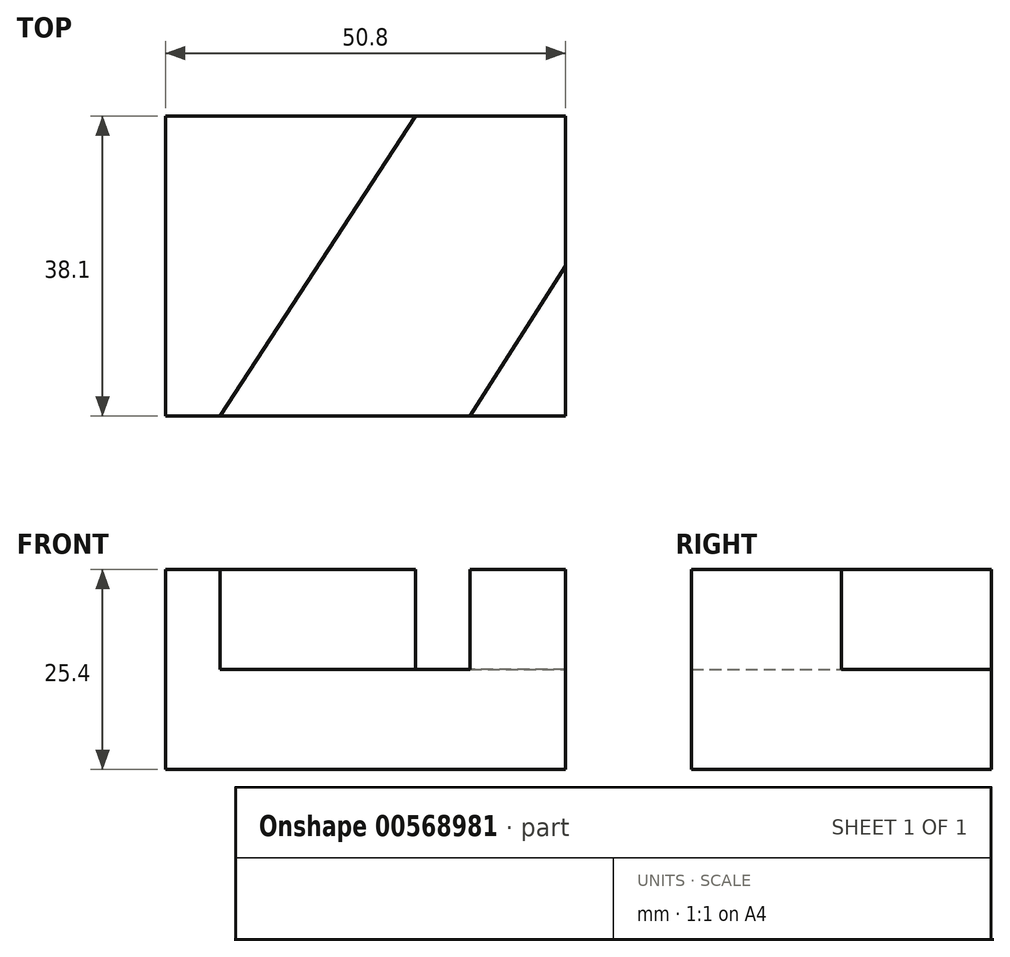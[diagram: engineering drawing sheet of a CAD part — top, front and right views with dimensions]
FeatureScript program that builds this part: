
annotation { "Feature Type Name" : "Feature", "Feature Type Description" : "" }
export const myFeature = defineFeature(function(context is Context, id is Id, definition is map)
    precondition{}
    {
        {
            var Q0;
            Q0=qCreatedBy(makeId("Top.planeOp"),FACE);
            var sketch = newSketch(context, id + "F0", { "sketchPlane" : qUnion([Q0])});
            skLineSegment(sketch, "E0.bottom", {"start": v(-24.31, 27.23) * mm, "end": v(26.49, 27.23) * mm});
            skLineSegment(sketch, "E0.top", {"start": v(-24.31, -10.87) * mm, "end": v(26.49, -10.87) * mm});
            skLineSegment(sketch, "E0.left", {"start": v(-24.31, 27.23) * mm, "end": v(-24.31, -10.87) * mm});
            skLineSegment(sketch, "E0.right", {"start": v(26.49, 27.23) * mm, "end": v(26.49, -10.87) * mm});
            skSolve(sketch);
        }
        {
            var Q0;
            Q0 = qSketchRegion(id + "F0", true);
            extrude(context, id + "F1", {"entities" : qUnion([Q0]), "depth" : 25.4 * mm, "offsetDistance" : 25.4 * mm});
        }
        {
            var Q0;
            Q0=makeQuery(id+"F1.opExtrude","CAP_FACE",FACE,{"disambiguationData":[OSD([sQuery(id+"F0.wireOp",EDGE,"E0.bottom"),sQuery(id+"F0.wireOp",EDGE,"E0.top"),sQuery(id+"F0.wireOp",EDGE,"E0.left"),sQuery(id+"F0.wireOp",EDGE,"E0.right")])],"isStart":false});
            var sketch = newSketch(context, id + "F2", { "sketchPlane" : qUnion([Q0])});
            skLineSegment(sketch, "E1", {"start": v(-17.37, -10.87) * mm, "end": v(7.44, 27.23) * mm});
            skLineSegment(sketch, "E2", {"start": v(7.44, 27.23) * mm, "end": v(26.49, 27.23) * mm});
            skLineSegment(sketch, "E3", {"start": v(26.49, 27.23) * mm, "end": v(26.49, 8.18) * mm});
            skLineSegment(sketch, "E4", {"start": v(26.49, 8.18) * mm, "end": v(14.38, -10.87) * mm});
            skLineSegment(sketch, "E5", {"start": v(14.38, -10.87) * mm, "end": v(-17.37, -10.87) * mm});
            skSolve(sketch);
        }
        {
            var Q0;
            Q0=makeQuery(id+"F2.imprint","IMPRINT",FACE,{"disambiguationData":[TD([[makeQuery(id+"F2.imprint","IMPRINT",EDGE,{"derivedFrom":sQuery(id+"F2.wireOp",EDGE,"E1")}),-1.0]])]});
            var sketch = newSketch(context, id + "F3", { "sketchPlane" : qUnion([Q0])});
            skSolve(sketch);
        }
        {
            var Q0;
            Q0 = qSketchRegion(id + "F3", true);
            var Q1;
            Q1=makeQuery(id+"F2.imprint","IMPRINT",FACE,{"disambiguationData":[TD([[makeQuery(id+"F2.imprint","IMPRINT",EDGE,{"derivedFrom":sQuery(id+"F2.wireOp",EDGE,"E1")}),-1.0]])]});
            extrude(context, id + "F4", {"entities" : qUnion([Q0, Q1]), "operationType" : NewBodyOperationType.REMOVE, "oppositeDirection" : true, "depth" : 12.7 * mm, "offsetDistance" : 25.4 * mm});
        }
    });
